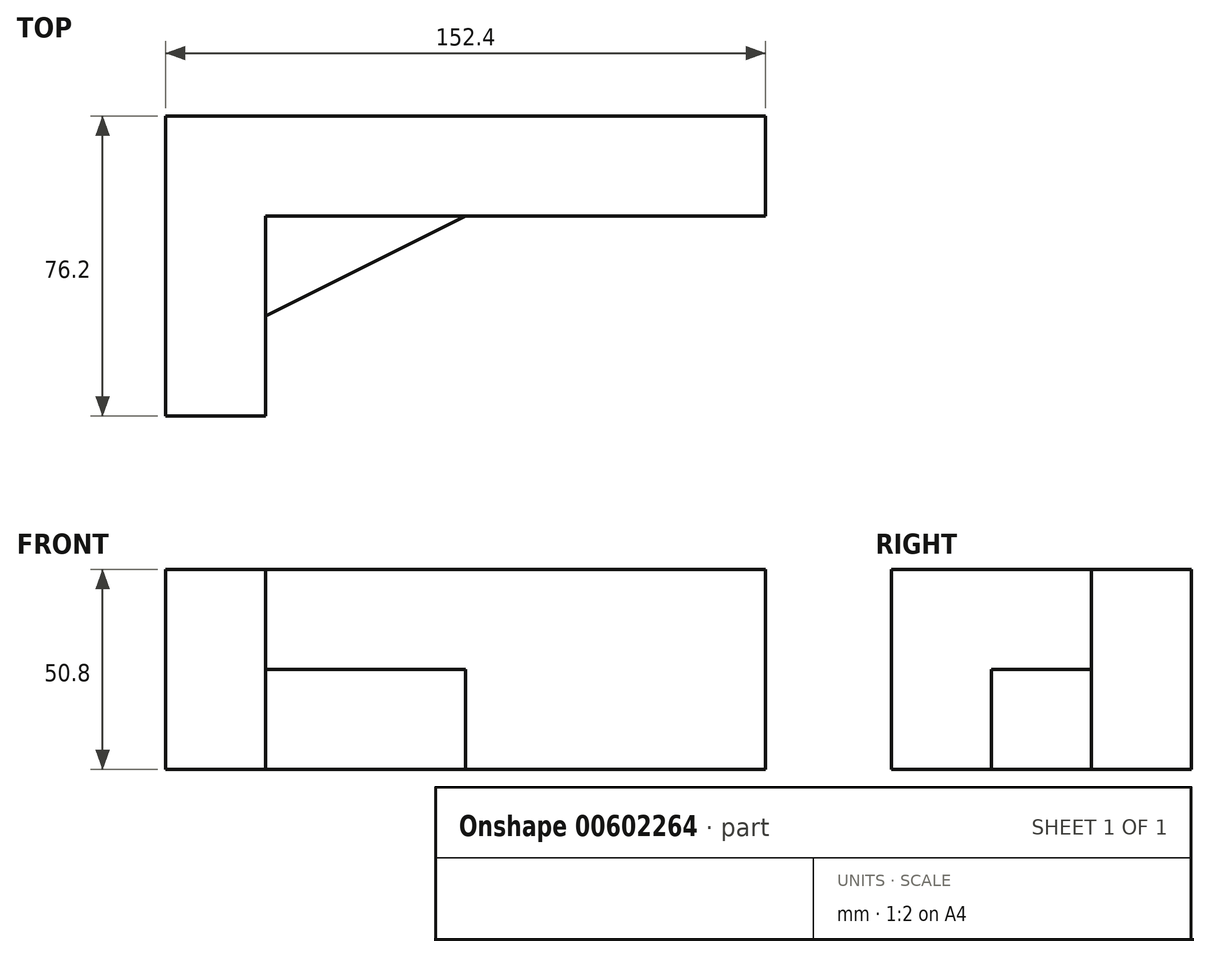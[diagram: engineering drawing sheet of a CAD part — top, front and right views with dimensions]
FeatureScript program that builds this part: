
annotation { "Feature Type Name" : "Feature", "Feature Type Description" : "" }
export const myFeature = defineFeature(function(context is Context, id is Id, definition is map)
    precondition{}
    {
        {
            var Q0;
            Q0=qCreatedBy(makeId("Top.planeOp"),FACE);
            var sketch = newSketch(context, id + "F0", { "sketchPlane" : qUnion([Q0])});
            skLineSegment(sketch, "E0", {"start": v(20.87, 0) * mm, "end": v(20.87, 76.2) * mm});
            skLineSegment(sketch, "E1", {"start": v(20.87, 76.2) * mm, "end": v(173.27, 76.2) * mm});
            skLineSegment(sketch, "E2", {"start": v(173.27, 76.2) * mm, "end": v(173.27, 50.8) * mm});
            skLineSegment(sketch, "E3", {"start": v(173.27, 50.8) * mm, "end": v(46.27, 50.8) * mm});
            skLineSegment(sketch, "E4", {"start": v(46.27, 50.8) * mm, "end": v(46.27, 0) * mm});
            skLineSegment(sketch, "E5", {"start": v(46.27, 0) * mm, "end": v(20.87, 0) * mm});
            skSolve(sketch);
        }
        {
            var Q0;
            Q0=makeQuery(id+"F0.imprint","IMPRINT",FACE,{"disambiguationData":[TD([[makeQuery(id+"F0.imprint","IMPRINT",EDGE,{"derivedFrom":sQuery(id+"F0.wireOp",EDGE,"E0")}),-1.0]])]});
            extrude(context, id + "F1", {"entities" : qUnion([Q0]), "depth" : 50.8 * mm, "offsetDistance" : 25.4 * mm});
        }
        {
            var Q0;
            Q0=makeQuery(id+"F1.opExtrude","CAP_FACE",FACE,{"disambiguationData":[OSD([sQuery(id+"F0.wireOp",EDGE,"E0"),sQuery(id+"F0.wireOp",EDGE,"E1"),sQuery(id+"F0.wireOp",EDGE,"E2"),sQuery(id+"F0.wireOp",EDGE,"E3"),sQuery(id+"F0.wireOp",EDGE,"E4"),sQuery(id+"F0.wireOp",EDGE,"E5")])],"isStart":true});
            var sketch = newSketch(context, id + "F2", { "sketchPlane" : qUnion([Q0])});
            skLineSegment(sketch, "E6", {"start": v(46.27, 0) * mm, "end": v(46.27, -25.4) * mm});
            skLineSegment(sketch, "E7", {"start": v(173.27, -50.8) * mm, "end": v(97.07, -50.8) * mm});
            skLineSegment(sketch, "E8", {"start": v(46.27, -25.4) * mm, "end": v(97.07, -50.8) * mm});
            skLineSegment(sketch, "E9", {"start": v(97.07, -50.8) * mm, "end": v(46.27, -50.8) * mm});
            skLineSegment(sketch, "E10", {"start": v(46.27, -50.8) * mm, "end": v(46.27, -25.4) * mm});
            skSolve(sketch);
        }
        {
            var Q0;
            Q0=makeQuery(id+"F2.imprint","IMPRINT",FACE,{"disambiguationData":[TD([[makeQuery(id+"F2.imprint","IMPRINT",EDGE,{"derivedFrom":sQuery(id+"F2.wireOp",EDGE,"E8")}),-1.0]])]});
            extrude(context, id + "F3", {"entities" : qUnion([Q0]), "oppositeDirection" : true, "depth" : 25.4 * mm, "offsetDistance" : 25.4 * mm});
        }
    });
